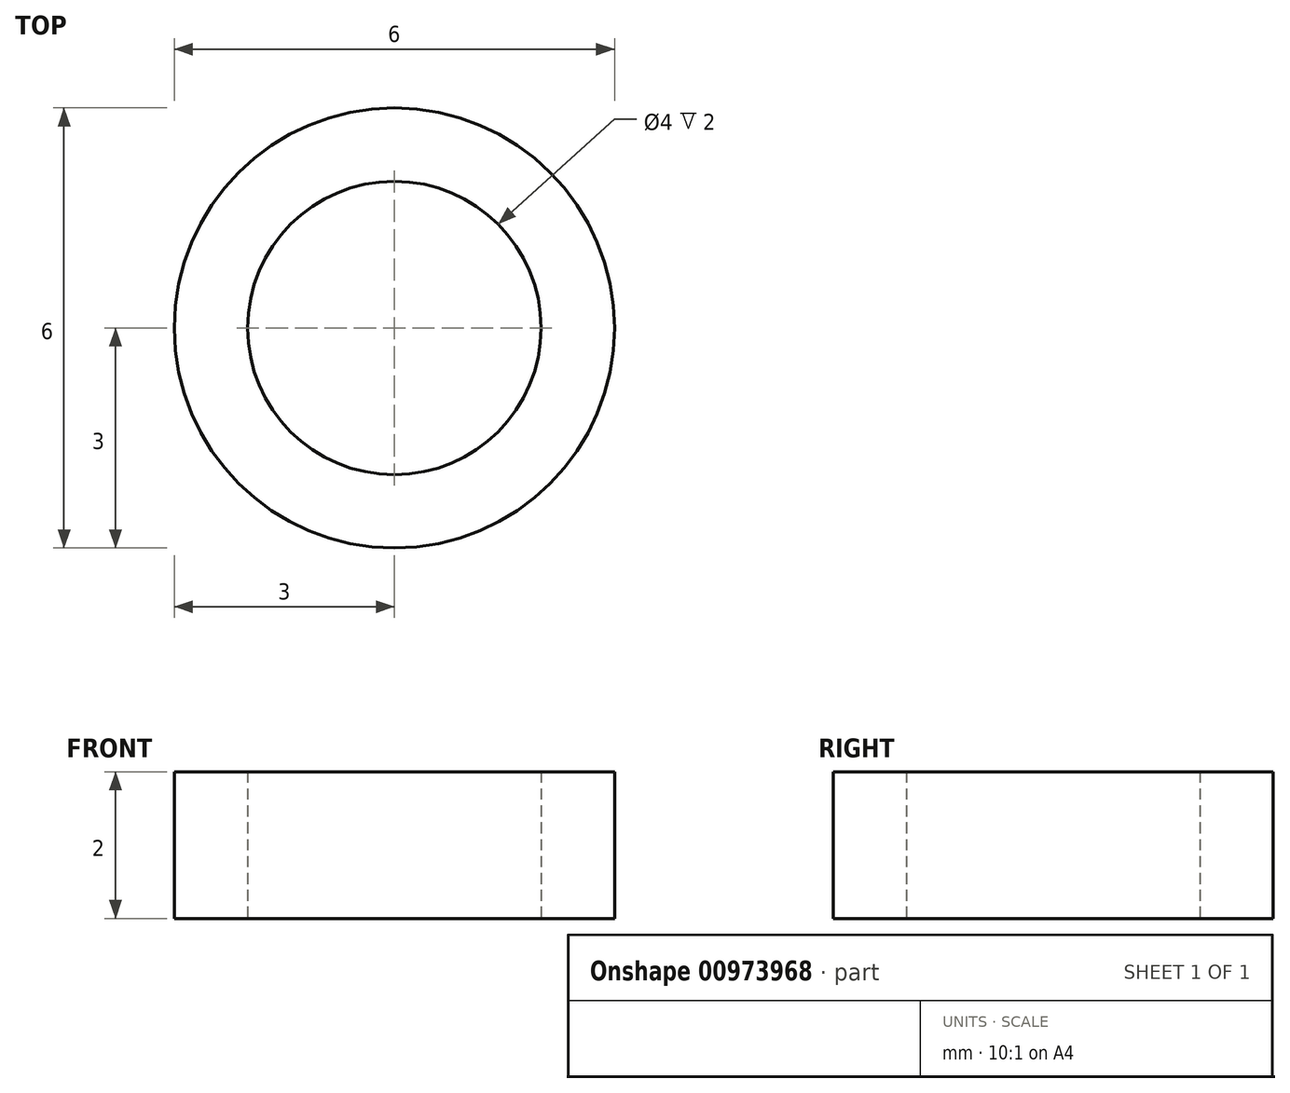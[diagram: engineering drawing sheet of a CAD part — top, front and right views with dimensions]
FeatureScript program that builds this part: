
annotation { "Feature Type Name" : "Feature", "Feature Type Description" : "" }
export const myFeature = defineFeature(function(context is Context, id is Id, definition is map)
    precondition{}
    {
        {
            var Q0;
            Q0=qCreatedBy(makeId("Top.planeOp"),FACE);
            var sketch = newSketch(context, id + "F0", { "sketchPlane" : qUnion([Q0])});
            skCircle(sketch, "E0", {"center": v(0, 0) * mm, "radius": 2 * mm});
            skCircle(sketch, "E1", {"center": v(0, 0) * mm, "radius": 3 * mm});
            skSolve(sketch);
        }
        {
            var Q0;
            Q0=makeQuery(id+"F0.imprint","IMPRINT",FACE,{"disambiguationData":[TD([[makeQuery(id+"F0.imprint","IMPRINT",EDGE,{"derivedFrom":sQuery(id+"F0.wireOp",EDGE,"E0")}),-1.0]])]});
            extrude(context, id + "F1", {"entities" : qUnion([Q0]), "depth" : 2 * mm, "offsetDistance" : 25 * mm});
        }
    });
